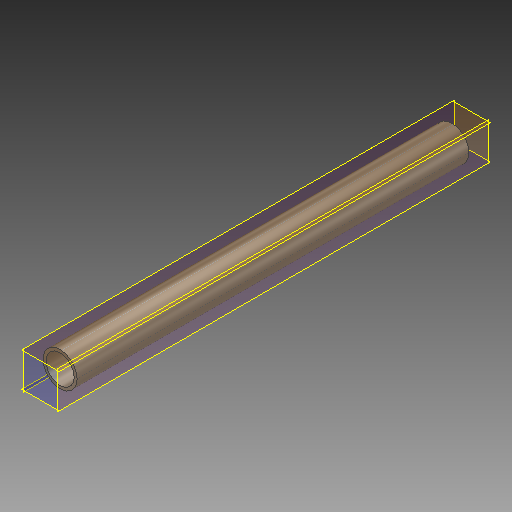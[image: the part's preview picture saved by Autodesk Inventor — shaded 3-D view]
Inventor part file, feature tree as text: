
AUTODESK INVENTOR PART (.ipt)
format: ipt  version: 2018 (Build 220112000, 112)  size: 105,472 bytes
history: native  units: mm
features: other x5, extrude x1, sketch x1
ambient origin geometry x8: Origin, YZ Plane, XZ Plane, XY Plane, X Axis, Y Axis, Z Axis, Center Point
bodies: Body1 (feature_tree)
feature tree (7):
  other  "ソリッド1"
  extrude  "押し出し1"  Depth=27.2mm
  other  "作業平面1"
  other  "作業平面2"
  other  "作業平面3"
  other  "作業平面4"
  sketch  "スケッチ1"
